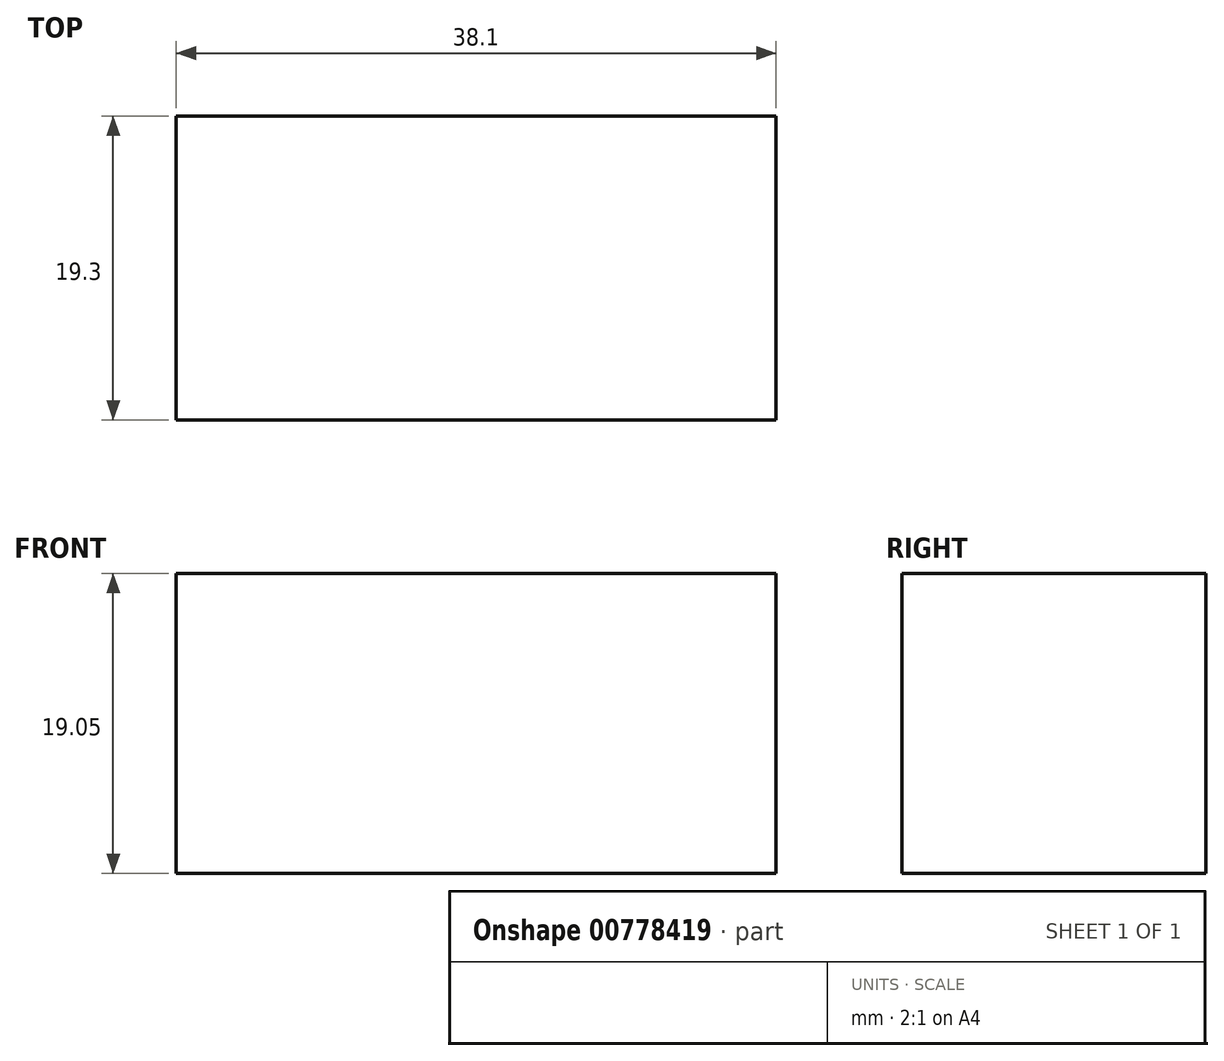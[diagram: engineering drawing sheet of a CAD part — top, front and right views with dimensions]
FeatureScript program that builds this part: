
annotation { "Feature Type Name" : "Feature", "Feature Type Description" : "" }
export const myFeature = defineFeature(function(context is Context, id is Id, definition is map)
    precondition{}
    {
        {
            var Q0;
            Q0=qCreatedBy(makeId("Front.planeOp"),FACE);
            var sketch = newSketch(context, id + "F0", { "sketchPlane" : qUnion([Q0])});
            skLineSegment(sketch, "E0.bottom", {"start": v(-12.4, 13.65) * mm, "end": v(25.7, 13.65) * mm});
            skLineSegment(sketch, "E0.top", {"start": v(-12.4, -5.4) * mm, "end": v(25.7, -5.4) * mm});
            skLineSegment(sketch, "E0.left", {"start": v(-12.4, 13.65) * mm, "end": v(-12.4, -5.4) * mm});
            skLineSegment(sketch, "E0.right", {"start": v(25.7, 13.65) * mm, "end": v(25.7, -5.4) * mm});
            skSolve(sketch);
        }
        {
            var Q0;
            Q0 = qSketchRegion(id + "F0", true);
            extrude(context, id + "F1", {"entities" : qUnion([Q0]), "oppositeDirection" : true, "depth" : 19.3 * mm, "offsetDistance" : 25.4 * mm});
        }
    });
